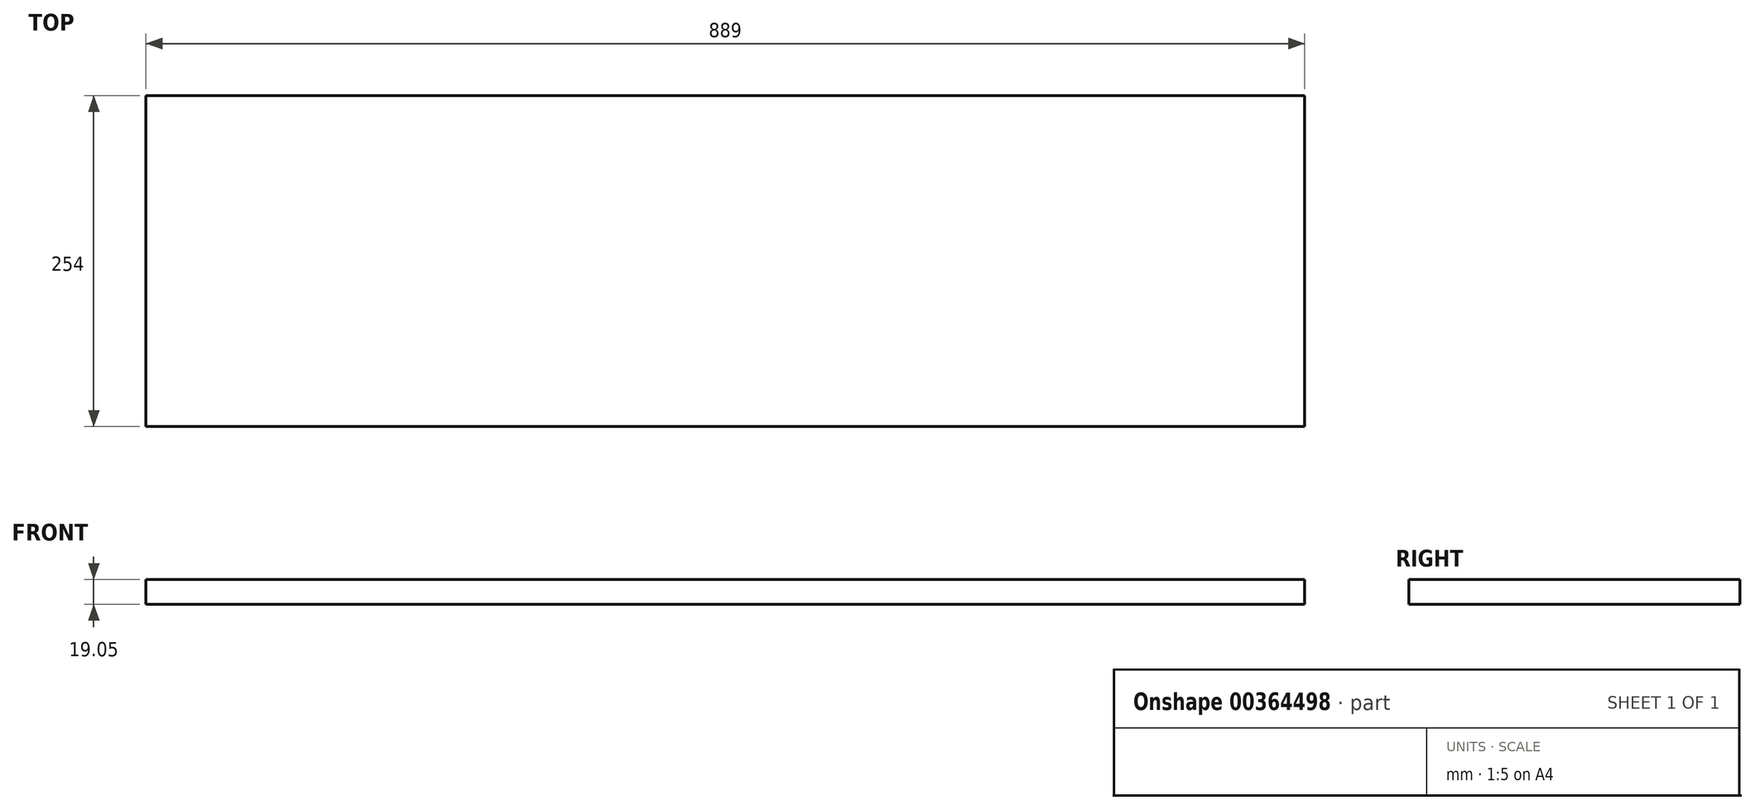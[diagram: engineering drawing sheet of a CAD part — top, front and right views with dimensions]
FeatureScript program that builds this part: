
annotation { "Feature Type Name" : "Feature", "Feature Type Description" : "" }
export const myFeature = defineFeature(function(context is Context, id is Id, definition is map)
    precondition{}
    {
        {
            var Q0;
            Q0=qCreatedBy(makeId("Top.planeOp"),FACE);
            var sketch = newSketch(context, id + "F0", { "sketchPlane" : qUnion([Q0])});
            skLineSegment(sketch, "E0.bottom", {"start": v(0, 0) * mm, "end": v(889, 0) * mm});
            skLineSegment(sketch, "E0.top", {"start": v(0, 254) * mm, "end": v(889, 254) * mm});
            skLineSegment(sketch, "E0.left", {"start": v(0, 0) * mm, "end": v(0, 254) * mm});
            skLineSegment(sketch, "E0.right", {"start": v(889, 0) * mm, "end": v(889, 254) * mm});
            skSolve(sketch);
        }
        {
            var Q0;
            Q0=qSketchRegion(id+"F0",true);
            extrude(context, id + "F1", {"entities" : qUnion([Q0]), "depth" : 19.05 * mm});
        }
    });
